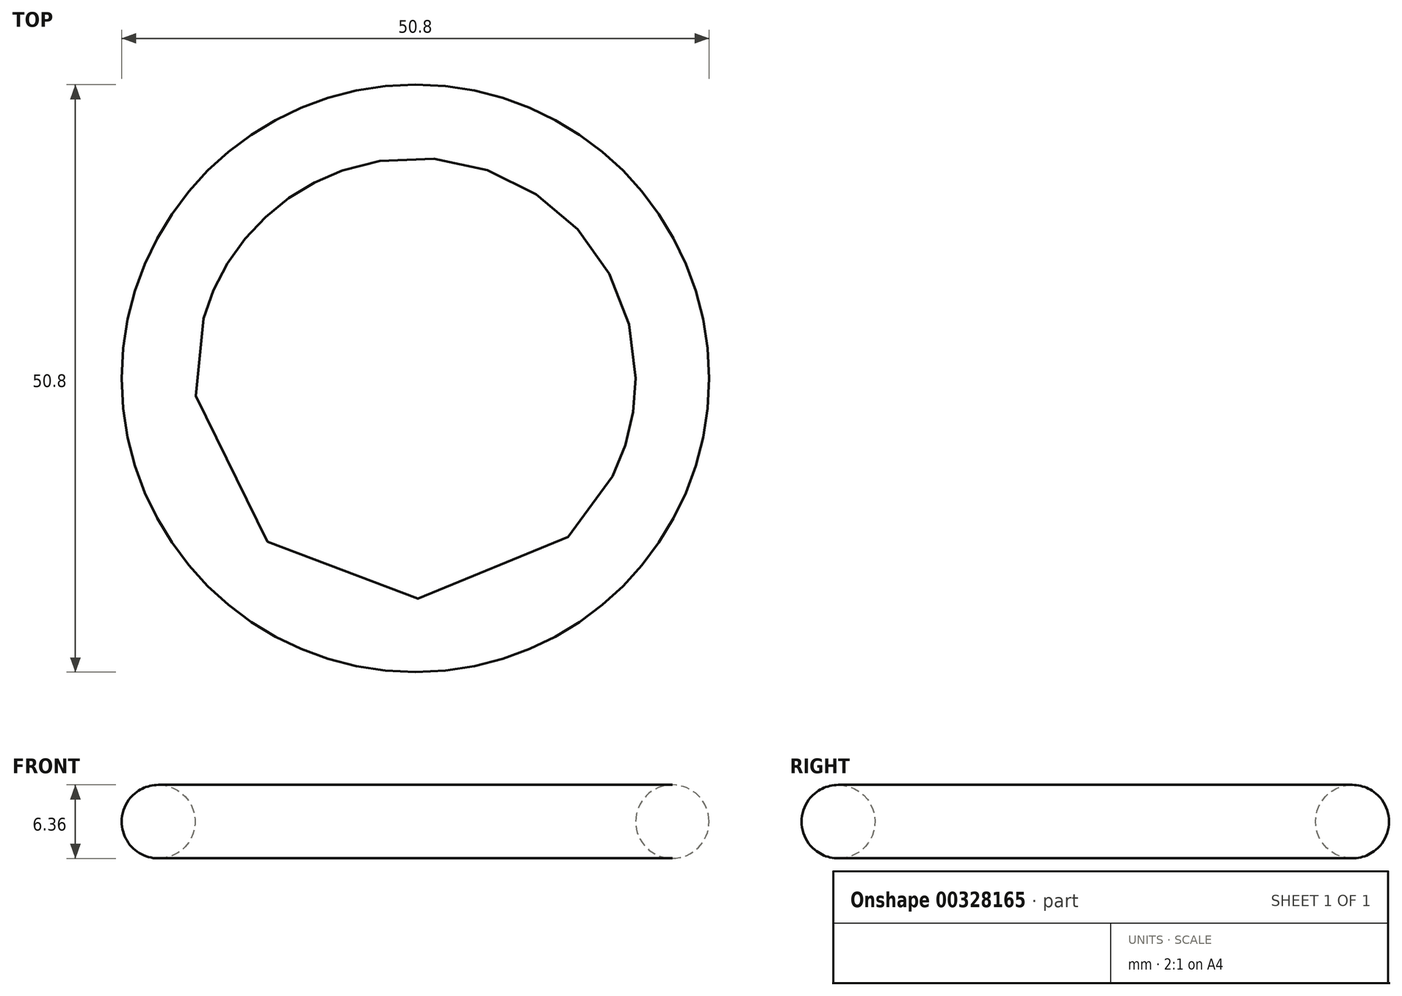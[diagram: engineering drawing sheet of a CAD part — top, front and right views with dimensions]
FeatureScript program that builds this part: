
annotation { "Feature Type Name" : "Feature", "Feature Type Description" : "" }
export const myFeature = defineFeature(function(context is Context, id is Id, definition is map)
    precondition{}
    {
        {
            var Q0;
            Q0=qCreatedBy(makeId("Front.planeOp"),FACE);
            var sketch = newSketch(context, id + "F0", { "sketchPlane" : qUnion([Q0])});
            skCircle(sketch, "E0", {"center": v(-22.23, 0) * mm, "radius": 3.18 * mm});
            skLineSegment(sketch, "E1", {"start": v(0, 9.08) * mm, "end": v(0, -6.91) * mm, "construction": true});
            skSolve(sketch);
        }
        {
            var Q0;
            Q0 = qSketchRegion(id + "F0", true);
            var Q1;
            Q1=sQuery(id+"F0.wireOp",EDGE,"E1");
            revolve(context, id + "F1", {"entities" : qUnion([Q0]), "axis" : qUnion([Q1]), "revolveType" : RevolveType.FULL});
        }
    });
